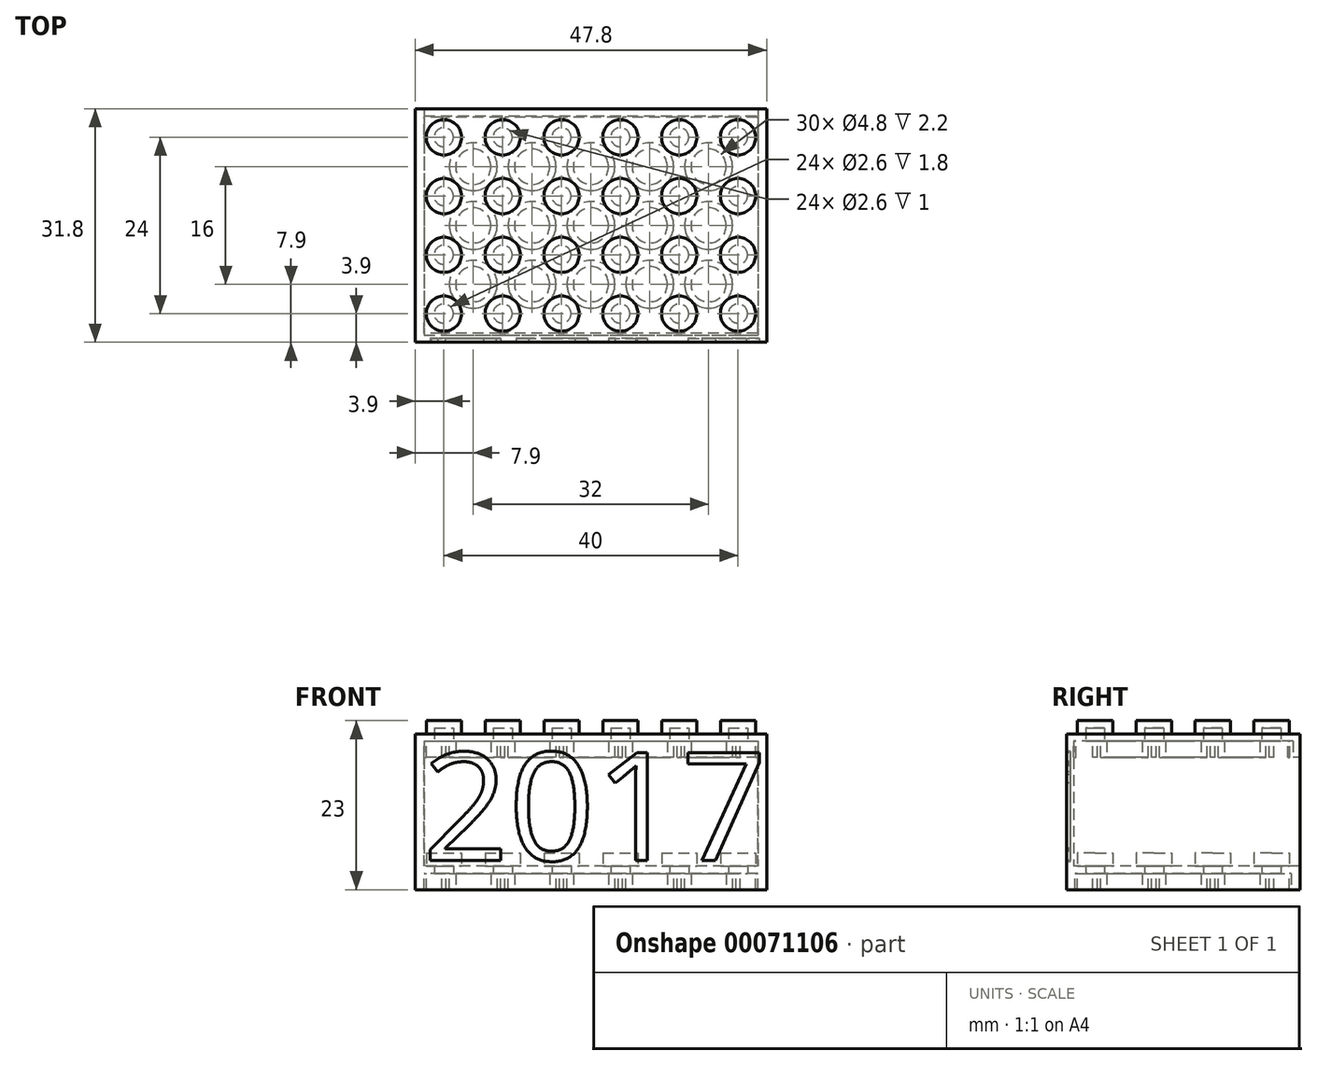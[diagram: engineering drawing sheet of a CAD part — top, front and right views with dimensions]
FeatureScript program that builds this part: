
annotation { "Feature Type Name" : "Feature", "Feature Type Description" : "" }
export const myFeature = defineFeature(function(context is Context, id is Id, definition is map)
    precondition{}
    {
        {
            var Q0;
            Q0=qCreatedBy(makeId("Top.planeOp"),FACE);
            var sketch = newSketch(context, id + "F0", { "sketchPlane" : qUnion([Q0])});
            skLineSegment(sketch, "E0.rect.bottom", {"start": v(23.9, 15.9) * mm, "end": v(-23.9, 15.9) * mm});
            skLineSegment(sketch, "E0.rect.top", {"start": v(23.9, -15.9) * mm, "end": v(-23.9, -15.9) * mm});
            skLineSegment(sketch, "E0.rect.left", {"start": v(23.9, 15.9) * mm, "end": v(23.9, -15.9) * mm});
            skLineSegment(sketch, "E0.rect.right", {"start": v(-23.9, 15.9) * mm, "end": v(-23.9, -15.9) * mm});
            skPoint(sketch, "E0.rect.middle", {"position": v(0, 0) * mm});
            skSolve(sketch);
        }
        {
            var Q0;
            Q0 = qSketchRegion(id + "F0", true);
            extrude(context, id + "F1", {"entities" : qUnion([Q0]), "depth" : 21.2 * mm});
        }
        {
            var Q0;
            Q0=makeQuery(id+"F1.opExtrude","CAP_FACE",FACE,{"disambiguationData":[OSD([sQuery(id+"F0.wireOp",EDGE,"E0.rect.bottom"),sQuery(id+"F0.wireOp",EDGE,"E0.rect.top"),sQuery(id+"F0.wireOp",EDGE,"E0.rect.left"),sQuery(id+"F0.wireOp",EDGE,"E0.rect.right")])],"isStart":false});
            var sketch = newSketch(context, id + "F2", { "sketchPlane" : qUnion([Q0])});
            skCircle(sketch, "E1", {"center": v(-20, 12) * mm, "radius": 2.4 * mm});
            skCircle(sketch, "E2.0.1.0", {"center": v(-20, 4) * mm, "radius": 2.4 * mm});
            skCircle(sketch, "E2.0.2.0", {"center": v(-20, -4) * mm, "radius": 2.4 * mm});
            skCircle(sketch, "E2.0.3.0", {"center": v(-20, -12) * mm, "radius": 2.4 * mm});
            skCircle(sketch, "E2.1.0.0", {"center": v(-12, 12) * mm, "radius": 2.4 * mm});
            skCircle(sketch, "E2.1.1.0", {"center": v(-12, 4) * mm, "radius": 2.4 * mm});
            skCircle(sketch, "E2.1.2.0", {"center": v(-12, -4) * mm, "radius": 2.4 * mm});
            skCircle(sketch, "E2.1.3.0", {"center": v(-12, -12) * mm, "radius": 2.4 * mm});
            skCircle(sketch, "E2.2.0.0", {"center": v(-4, 12) * mm, "radius": 2.4 * mm});
            skCircle(sketch, "E2.2.1.0", {"center": v(-4, 4) * mm, "radius": 2.4 * mm});
            skCircle(sketch, "E2.2.2.0", {"center": v(-4, -4) * mm, "radius": 2.4 * mm});
            skCircle(sketch, "E2.2.3.0", {"center": v(-4, -12) * mm, "radius": 2.4 * mm});
            skCircle(sketch, "E2.3.0.0", {"center": v(4, 12) * mm, "radius": 2.4 * mm});
            skCircle(sketch, "E2.3.1.0", {"center": v(4, 4) * mm, "radius": 2.4 * mm});
            skCircle(sketch, "E2.3.2.0", {"center": v(4, -4) * mm, "radius": 2.4 * mm});
            skCircle(sketch, "E2.3.3.0", {"center": v(4, -12) * mm, "radius": 2.4 * mm});
            skCircle(sketch, "E2.4.0.0", {"center": v(12, 12) * mm, "radius": 2.4 * mm});
            skCircle(sketch, "E2.4.1.0", {"center": v(12, 4) * mm, "radius": 2.4 * mm});
            skCircle(sketch, "E2.4.2.0", {"center": v(12, -4) * mm, "radius": 2.4 * mm});
            skCircle(sketch, "E2.4.3.0", {"center": v(12, -12) * mm, "radius": 2.4 * mm});
            skCircle(sketch, "E2.5.0.0", {"center": v(20, 12) * mm, "radius": 2.4 * mm});
            skCircle(sketch, "E2.5.1.0", {"center": v(20, 4) * mm, "radius": 2.4 * mm});
            skCircle(sketch, "E2.5.2.0", {"center": v(20, -4) * mm, "radius": 2.4 * mm});
            skCircle(sketch, "E2.5.3.0", {"center": v(20, -12) * mm, "radius": 2.4 * mm});
            skLineSegment(sketch, "E2.direction1", {"start": v(-20, 12) * mm, "end": v(-12, 12) * mm, "construction": true});
            skLineSegment(sketch, "E2.direction2", {"start": v(-20, 12) * mm, "end": v(-20, 4) * mm, "construction": true});
            skLineSegment(sketch, "E3", {"start": v(-12, 12) * mm, "end": v(-20, 4) * mm, "construction": true});
            skLineSegment(sketch, "E4", {"start": v(-4, 12) * mm, "end": v(-20, -4) * mm, "construction": true});
            skLineSegment(sketch, "E5", {"start": v(4, 12) * mm, "end": v(-20, -12) * mm, "construction": true});
            skLineSegment(sketch, "E6", {"start": v(12, 12) * mm, "end": v(-12, -12) * mm, "construction": true});
            skLineSegment(sketch, "E7", {"start": v(20, 12) * mm, "end": v(-4, -12) * mm, "construction": true});
            skLineSegment(sketch, "E8", {"start": v(20, 4) * mm, "end": v(4, -12) * mm, "construction": true});
            skLineSegment(sketch, "E9", {"start": v(20, -4) * mm, "end": v(12, -12) * mm, "construction": true});
            skLineSegment(sketch, "E10", {"start": v(20, 4) * mm, "end": v(12, 12) * mm, "construction": true});
            skLineSegment(sketch, "E11", {"start": v(20, -4) * mm, "end": v(4, 12) * mm, "construction": true});
            skLineSegment(sketch, "E12", {"start": v(20, -12) * mm, "end": v(-4, 12) * mm, "construction": true});
            skLineSegment(sketch, "E13", {"start": v(12, -12) * mm, "end": v(-12, 12) * mm, "construction": true});
            skLineSegment(sketch, "E14", {"start": v(4, -12) * mm, "end": v(-20, 12) * mm, "construction": true});
            skLineSegment(sketch, "E15", {"start": v(-4, -12) * mm, "end": v(-20, 4) * mm, "construction": true});
            skLineSegment(sketch, "E16", {"start": v(-12, -12) * mm, "end": v(-20, -4) * mm, "construction": true});
            skLineSegment(sketch, "E17", {"start": v(20, 12) * mm, "end": v(-38.07, 12) * mm, "construction": true});
            skLineSegment(sketch, "E18", {"start": v(-38.07, 12) * mm, "end": v(32, 12) * mm, "construction": true});
            skLineSegment(sketch, "E19", {"start": v(32, 12) * mm, "end": v(20, 12) * mm, "construction": true});
            skLineSegment(sketch, "E20", {"start": v(20, -12) * mm, "end": v(20, 35.87) * mm, "construction": true});
            skLineSegment(sketch, "E21", {"start": v(20, 35.87) * mm, "end": v(20, -18.4) * mm, "construction": true});
            skLineSegment(sketch, "E22", {"start": v(20, -18.4) * mm, "end": v(20, -12) * mm, "construction": true});
            skLineSegment(sketch, "E23", {"start": v(20, -12) * mm, "end": v(-45.19, -12) * mm, "construction": true});
            skLineSegment(sketch, "E24", {"start": v(-45.19, -12) * mm, "end": v(30.07, -12) * mm, "construction": true});
            skLineSegment(sketch, "E25", {"start": v(30.07, -12) * mm, "end": v(20, -12) * mm, "construction": true});
            skLineSegment(sketch, "E26", {"start": v(20, -4) * mm, "end": v(-32.13, -4) * mm, "construction": true});
            skLineSegment(sketch, "E27", {"start": v(-32.13, -4) * mm, "end": v(29.65, -4) * mm, "construction": true});
            skLineSegment(sketch, "E28", {"start": v(29.65, -4) * mm, "end": v(20, -4) * mm, "construction": true});
            skLineSegment(sketch, "E29", {"start": v(20, 4) * mm, "end": v(-52.97, 4) * mm, "construction": true});
            skLineSegment(sketch, "E30", {"start": v(-52.97, 4) * mm, "end": v(40.27, 4) * mm, "construction": true});
            skLineSegment(sketch, "E31", {"start": v(40.27, 4) * mm, "end": v(20, 4) * mm, "construction": true});
            skLineSegment(sketch, "E32", {"start": v(12, 12) * mm, "end": v(12, -18.88) * mm, "construction": true});
            skLineSegment(sketch, "E33", {"start": v(12, -18.88) * mm, "end": v(12, 25.65) * mm, "construction": true});
            skLineSegment(sketch, "E34", {"start": v(12, 25.65) * mm, "end": v(12, 12) * mm, "construction": true});
            skLineSegment(sketch, "E35", {"start": v(4, 12) * mm, "end": v(4, -22.99) * mm, "construction": true});
            skLineSegment(sketch, "E36", {"start": v(4, -22.99) * mm, "end": v(4, 30.25) * mm, "construction": true});
            skLineSegment(sketch, "E37", {"start": v(4, 30.25) * mm, "end": v(4, 12) * mm, "construction": true});
            skLineSegment(sketch, "E38", {"start": v(-4, 12) * mm, "end": v(-4, -21.1) * mm, "construction": true});
            skLineSegment(sketch, "E39", {"start": v(-4, -21.1) * mm, "end": v(-4, 37.53) * mm, "construction": true});
            skLineSegment(sketch, "E40", {"start": v(-4, 37.53) * mm, "end": v(-4, 12) * mm, "construction": true});
            skLineSegment(sketch, "E41", {"start": v(-12, 12) * mm, "end": v(-12, -21.86) * mm, "construction": true});
            skLineSegment(sketch, "E42", {"start": v(-12, -21.86) * mm, "end": v(-12, 28.01) * mm, "construction": true});
            skLineSegment(sketch, "E43", {"start": v(-12, 28.01) * mm, "end": v(-12, 12) * mm, "construction": true});
            skLineSegment(sketch, "E44", {"start": v(-20, 12) * mm, "end": v(-20, -23.6) * mm, "construction": true});
            skLineSegment(sketch, "E45", {"start": v(-20, -23.6) * mm, "end": v(-20, 37.01) * mm, "construction": true});
            skSolve(sketch);
        }
        {
            var Q0;
            Q0 = qSketchRegion(id + "F2", true);
            extrude(context, id + "F3", {"entities" : qUnion([Q0]), "operationType" : NewBodyOperationType.ADD, "depth" : 1.8 * mm});
        }
        {
            var Q0;
            Q0=makeQuery(id+"F1.opExtrude","SWEPT_FACE",FACE,{"disambiguationData":[OSD([sQuery(id+"F0.wireOp",EDGE,"E0.rect.top")])]});
            var sketch = newSketch(context, id + "F4", { "sketchPlane" : qUnion([Q0])});
            skLineSegment(sketch, "E46.bottom", {"start": v(-22.7, 18) * mm, "end": v(22.7, 18) * mm});
            skLineSegment(sketch, "E46.top", {"start": v(-22.7, 3.2) * mm, "end": v(22.7, 3.2) * mm});
            skLineSegment(sketch, "E46.left", {"start": v(-22.7, 18) * mm, "end": v(-22.7, 3.2) * mm});
            skLineSegment(sketch, "E46.right", {"start": v(22.7, 18) * mm, "end": v(22.7, 3.2) * mm});
            skSolve(sketch);
        }
        {
            var Q0;
            Q0 = qSketchRegion(id + "F4", true);
            extrude(context, id + "F5", {"entities" : qUnion([Q0]), "operationType" : NewBodyOperationType.REMOVE, "endBound" : BoundingType.UP_TO_NEXT, "oppositeDirection" : true, "depth" : 25 * mm});
        }
        {
            var Q0;
            Q0=makeQuery(id+"F5.boolean.opBoolean","COPY",FACE,{"derivedFrom":makeQuery(id+"F5.opExtrude","SWEPT_FACE",FACE,{"disambiguationData":[OSD([sQuery(id+"F4.wireOp",EDGE,"E46.bottom")])]})});
            var sketch = newSketch(context, id + "F6", { "sketchPlane" : qUnion([Q0])});
            skLineSegment(sketch, "E47.bottom", {"start": v(-22.7, 14.9) * mm, "end": v(22.7, 14.9) * mm});
            skLineSegment(sketch, "E47.top", {"start": v(-22.7, -14.9) * mm, "end": v(22.7, -14.9) * mm});
            skLineSegment(sketch, "E47.left", {"start": v(-22.7, 14.9) * mm, "end": v(-22.7, -14.9) * mm});
            skLineSegment(sketch, "E47.right", {"start": v(22.7, 14.9) * mm, "end": v(22.7, -14.9) * mm});
            skSolve(sketch);
        }
        {
            var Q0;
            Q0 = qSketchRegion(id + "F6", true);
            extrude(context, id + "F7", {"entities" : qUnion([Q0]), "operationType" : NewBodyOperationType.REMOVE, "oppositeDirection" : true, "depth" : 2.2 * mm});
        }
        {
            var Q0;
            Q0=makeQuery(id+"F7.boolean.opBoolean","COPY",FACE,{"derivedFrom":makeQuery(id+"F7.opExtrude","CAP_FACE",FACE,{"disambiguationData":[OSD([sQuery(id+"F6.wireOp",EDGE,"E47.bottom"),sQuery(id+"F6.wireOp",EDGE,"E47.top"),sQuery(id+"F6.wireOp",EDGE,"E47.left"),sQuery(id+"F6.wireOp",EDGE,"E47.right")])],"isStart":false})});
            var sketch = newSketch(context, id + "F8", { "sketchPlane" : qUnion([Q0])});
            skCircle(sketch, "E48", {"center": v(-20, 12) * mm, "radius": 1.3 * mm});
            skCircle(sketch, "E49.0.1.0", {"center": v(-20, 4) * mm, "radius": 1.3 * mm});
            skCircle(sketch, "E49.0.2.0", {"center": v(-20, -4) * mm, "radius": 1.3 * mm});
            skCircle(sketch, "E49.0.3.0", {"center": v(-20, -12) * mm, "radius": 1.3 * mm});
            skCircle(sketch, "E49.1.0.0", {"center": v(-12, 12) * mm, "radius": 1.3 * mm});
            skCircle(sketch, "E49.1.1.0", {"center": v(-12, 4) * mm, "radius": 1.3 * mm});
            skCircle(sketch, "E49.1.2.0", {"center": v(-12, -4) * mm, "radius": 1.3 * mm});
            skCircle(sketch, "E49.1.3.0", {"center": v(-12, -12) * mm, "radius": 1.3 * mm});
            skCircle(sketch, "E49.2.0.0", {"center": v(-4, 12) * mm, "radius": 1.3 * mm});
            skCircle(sketch, "E49.2.1.0", {"center": v(-4, 4) * mm, "radius": 1.3 * mm});
            skCircle(sketch, "E49.2.2.0", {"center": v(-4, -4) * mm, "radius": 1.3 * mm});
            skCircle(sketch, "E49.2.3.0", {"center": v(-4, -12) * mm, "radius": 1.3 * mm});
            skCircle(sketch, "E49.3.0.0", {"center": v(4, 12) * mm, "radius": 1.3 * mm});
            skCircle(sketch, "E49.3.1.0", {"center": v(4, 4) * mm, "radius": 1.3 * mm});
            skCircle(sketch, "E49.3.2.0", {"center": v(4, -4) * mm, "radius": 1.3 * mm});
            skCircle(sketch, "E49.3.3.0", {"center": v(4, -12) * mm, "radius": 1.3 * mm});
            skCircle(sketch, "E49.4.0.0", {"center": v(12, 12) * mm, "radius": 1.3 * mm});
            skCircle(sketch, "E49.4.1.0", {"center": v(12, 4) * mm, "radius": 1.3 * mm});
            skCircle(sketch, "E49.4.2.0", {"center": v(12, -4) * mm, "radius": 1.3 * mm});
            skCircle(sketch, "E49.4.3.0", {"center": v(12, -12) * mm, "radius": 1.3 * mm});
            skCircle(sketch, "E49.5.0.0", {"center": v(20, 12) * mm, "radius": 1.3 * mm});
            skCircle(sketch, "E49.5.1.0", {"center": v(20, 4) * mm, "radius": 1.3 * mm});
            skCircle(sketch, "E49.5.2.0", {"center": v(20, -4) * mm, "radius": 1.3 * mm});
            skCircle(sketch, "E49.5.3.0", {"center": v(20, -12) * mm, "radius": 1.3 * mm});
            skLineSegment(sketch, "E49.direction1", {"start": v(-20, 12) * mm, "end": v(-12, 12) * mm, "construction": true});
            skLineSegment(sketch, "E49.direction2", {"start": v(-20, 12) * mm, "end": v(-20, 4) * mm, "construction": true});
            skSolve(sketch);
        }
        {
            var Q0;
            Q0 = qSketchRegion(id + "F8", true);
            extrude(context, id + "F9", {"entities" : qUnion([Q0]), "operationType" : NewBodyOperationType.REMOVE, "oppositeDirection" : true, "depth" : 1.8 * mm});
        }
        {
            var Q0;
            Q0=makeQuery(id+"F5.boolean.opBoolean","COPY",FACE,{"derivedFrom":makeQuery(id+"F5.opExtrude","SWEPT_FACE",FACE,{"disambiguationData":[OSD([sQuery(id+"F4.wireOp",EDGE,"E46.top")])]})});
            var sketch = newSketch(context, id + "F10", { "sketchPlane" : qUnion([Q0])});
            skCircle(sketch, "E50", {"center": v(-20, 12) * mm, "radius": 2.4 * mm});
            skCircle(sketch, "E51.0.1.0", {"center": v(-20, 4) * mm, "radius": 2.4 * mm});
            skCircle(sketch, "E51.0.2.0", {"center": v(-20, -4) * mm, "radius": 2.4 * mm});
            skCircle(sketch, "E51.0.3.0", {"center": v(-20, -12) * mm, "radius": 2.4 * mm});
            skCircle(sketch, "E51.1.0.0", {"center": v(-12, 12) * mm, "radius": 2.4 * mm});
            skCircle(sketch, "E51.1.1.0", {"center": v(-12, 4) * mm, "radius": 2.4 * mm});
            skCircle(sketch, "E51.1.2.0", {"center": v(-12, -4) * mm, "radius": 2.4 * mm});
            skCircle(sketch, "E51.1.3.0", {"center": v(-12, -12) * mm, "radius": 2.4 * mm});
            skCircle(sketch, "E51.2.0.0", {"center": v(-4, 12) * mm, "radius": 2.4 * mm});
            skCircle(sketch, "E51.2.1.0", {"center": v(-4, 4) * mm, "radius": 2.4 * mm});
            skCircle(sketch, "E51.2.2.0", {"center": v(-4, -4) * mm, "radius": 2.4 * mm});
            skCircle(sketch, "E51.2.3.0", {"center": v(-4, -12) * mm, "radius": 2.4 * mm});
            skCircle(sketch, "E51.3.0.0", {"center": v(4, 12) * mm, "radius": 2.4 * mm});
            skCircle(sketch, "E51.3.1.0", {"center": v(4, 4) * mm, "radius": 2.4 * mm});
            skCircle(sketch, "E51.3.2.0", {"center": v(4, -4) * mm, "radius": 2.4 * mm});
            skCircle(sketch, "E51.3.3.0", {"center": v(4, -12) * mm, "radius": 2.4 * mm});
            skCircle(sketch, "E51.4.0.0", {"center": v(12, 12) * mm, "radius": 2.4 * mm});
            skCircle(sketch, "E51.4.1.0", {"center": v(12, 4) * mm, "radius": 2.4 * mm});
            skCircle(sketch, "E51.4.2.0", {"center": v(12, -4) * mm, "radius": 2.4 * mm});
            skCircle(sketch, "E51.4.3.0", {"center": v(12, -12) * mm, "radius": 2.4 * mm});
            skCircle(sketch, "E51.5.0.0", {"center": v(20, 12) * mm, "radius": 2.4 * mm});
            skCircle(sketch, "E51.5.1.0", {"center": v(20, 4) * mm, "radius": 2.4 * mm});
            skCircle(sketch, "E51.5.2.0", {"center": v(20, -4) * mm, "radius": 2.4 * mm});
            skCircle(sketch, "E51.5.3.0", {"center": v(20, -12) * mm, "radius": 2.4 * mm});
            skLineSegment(sketch, "E51.direction1", {"start": v(-20, 12) * mm, "end": v(-12, 12) * mm, "construction": true});
            skLineSegment(sketch, "E51.direction2", {"start": v(-20, 12) * mm, "end": v(-20, 4) * mm, "construction": true});
            skSolve(sketch);
        }
        {
            var Q0;
            Q0 = qSketchRegion(id + "F10", true);
            extrude(context, id + "F11", {"entities" : qUnion([Q0]), "operationType" : NewBodyOperationType.ADD, "depth" : 1.8 * mm});
        }
        {
            var Q0;
            Q0=makeQuery(id+"F1.opExtrude","CAP_FACE",FACE,{"disambiguationData":[OSD([sQuery(id+"F0.wireOp",EDGE,"E0.rect.bottom"),sQuery(id+"F0.wireOp",EDGE,"E0.rect.top"),sQuery(id+"F0.wireOp",EDGE,"E0.rect.left"),sQuery(id+"F0.wireOp",EDGE,"E0.rect.right")])],"isStart":true});
            var sketch = newSketch(context, id + "F12", { "sketchPlane" : qUnion([Q0])});
            skLineSegment(sketch, "E52.rect.bottom", {"start": v(22.7, 14.7) * mm, "end": v(-22.7, 14.7) * mm});
            skLineSegment(sketch, "E52.rect.top", {"start": v(22.7, -14.7) * mm, "end": v(-22.7, -14.7) * mm});
            skLineSegment(sketch, "E52.rect.left", {"start": v(22.7, 14.7) * mm, "end": v(22.7, -14.7) * mm});
            skLineSegment(sketch, "E52.rect.right", {"start": v(-22.7, 14.7) * mm, "end": v(-22.7, -14.7) * mm});
            skPoint(sketch, "E52.rect.middle", {"position": v(0, 0) * mm});
            skSolve(sketch);
        }
        {
            var Q0;
            Q0 = qSketchRegion(id + "F12", true);
            extrude(context, id + "F13", {"entities" : qUnion([Q0]), "operationType" : NewBodyOperationType.REMOVE, "oppositeDirection" : true, "depth" : 2.2 * mm});
        }
        {
            var Q0;
            Q0=makeQuery(id+"F13.boolean.opBoolean","COPY",FACE,{"derivedFrom":makeQuery(id+"F13.opExtrude","CAP_FACE",FACE,{"disambiguationData":[OSD([sQuery(id+"F12.wireOp",EDGE,"E52.rect.bottom"),sQuery(id+"F12.wireOp",EDGE,"E52.rect.top"),sQuery(id+"F12.wireOp",EDGE,"E52.rect.left"),sQuery(id+"F12.wireOp",EDGE,"E52.rect.right")])],"isStart":false})});
            var sketch = newSketch(context, id + "F14", { "sketchPlane" : qUnion([Q0])});
            skCircle(sketch, "E53", {"center": v(-20, 12) * mm, "radius": 1.3 * mm});
            skCircle(sketch, "E54.0.1.0", {"center": v(-20, 4) * mm, "radius": 1.3 * mm});
            skCircle(sketch, "E54.0.2.0", {"center": v(-20, -4) * mm, "radius": 1.3 * mm});
            skCircle(sketch, "E54.0.3.0", {"center": v(-20, -12) * mm, "radius": 1.3 * mm});
            skCircle(sketch, "E54.1.0.0", {"center": v(-12, 12) * mm, "radius": 1.3 * mm});
            skCircle(sketch, "E54.1.1.0", {"center": v(-12, 4) * mm, "radius": 1.3 * mm});
            skCircle(sketch, "E54.1.2.0", {"center": v(-12, -4) * mm, "radius": 1.3 * mm});
            skCircle(sketch, "E54.1.3.0", {"center": v(-12, -12) * mm, "radius": 1.3 * mm});
            skCircle(sketch, "E54.2.0.0", {"center": v(-4, 12) * mm, "radius": 1.3 * mm});
            skCircle(sketch, "E54.2.1.0", {"center": v(-4, 4) * mm, "radius": 1.3 * mm});
            skCircle(sketch, "E54.2.2.0", {"center": v(-4, -4) * mm, "radius": 1.3 * mm});
            skCircle(sketch, "E54.2.3.0", {"center": v(-4, -12) * mm, "radius": 1.3 * mm});
            skCircle(sketch, "E54.3.0.0", {"center": v(4, 12) * mm, "radius": 1.3 * mm});
            skCircle(sketch, "E54.3.1.0", {"center": v(4, 4) * mm, "radius": 1.3 * mm});
            skCircle(sketch, "E54.3.2.0", {"center": v(4, -4) * mm, "radius": 1.3 * mm});
            skCircle(sketch, "E54.3.3.0", {"center": v(4, -12) * mm, "radius": 1.3 * mm});
            skCircle(sketch, "E54.4.0.0", {"center": v(12, 12) * mm, "radius": 1.3 * mm});
            skCircle(sketch, "E54.4.1.0", {"center": v(12, 4) * mm, "radius": 1.3 * mm});
            skCircle(sketch, "E54.4.2.0", {"center": v(12, -4) * mm, "radius": 1.3 * mm});
            skCircle(sketch, "E54.4.3.0", {"center": v(12, -12) * mm, "radius": 1.3 * mm});
            skCircle(sketch, "E54.5.0.0", {"center": v(20, 12) * mm, "radius": 1.3 * mm});
            skCircle(sketch, "E54.5.1.0", {"center": v(20, 4) * mm, "radius": 1.3 * mm});
            skCircle(sketch, "E54.5.2.0", {"center": v(20, -4) * mm, "radius": 1.3 * mm});
            skCircle(sketch, "E54.5.3.0", {"center": v(20, -12) * mm, "radius": 1.3 * mm});
            skLineSegment(sketch, "E54.direction1", {"start": v(-20, 12) * mm, "end": v(-12, 12) * mm, "construction": true});
            skLineSegment(sketch, "E54.direction2", {"start": v(-20, 12) * mm, "end": v(-20, 4) * mm, "construction": true});
            skLineSegment(sketch, "E55", {"start": v(4, -12) * mm, "end": v(-20, 12) * mm, "construction": true});
            skLineSegment(sketch, "E56", {"start": v(-4, -12) * mm, "end": v(-20, 4) * mm, "construction": true});
            skLineSegment(sketch, "E57", {"start": v(-12, -12) * mm, "end": v(-20, -4) * mm, "construction": true});
            skLineSegment(sketch, "E58", {"start": v(12, -12) * mm, "end": v(-12, 12) * mm, "construction": true});
            skLineSegment(sketch, "E59", {"start": v(20, -12) * mm, "end": v(-4, 12) * mm, "construction": true});
            skLineSegment(sketch, "E60", {"start": v(20, -4) * mm, "end": v(4, 12) * mm, "construction": true});
            skLineSegment(sketch, "E61", {"start": v(20, 4) * mm, "end": v(12, 12) * mm, "construction": true});
            skLineSegment(sketch, "E62", {"start": v(20, -4) * mm, "end": v(12, -12) * mm, "construction": true});
            skLineSegment(sketch, "E63", {"start": v(20, 4) * mm, "end": v(4, -12) * mm, "construction": true});
            skLineSegment(sketch, "E64", {"start": v(-4, -12) * mm, "end": v(20, 12) * mm, "construction": true});
            skLineSegment(sketch, "E65", {"start": v(12, 12) * mm, "end": v(-12, -12) * mm, "construction": true});
            skLineSegment(sketch, "E66", {"start": v(4, 12) * mm, "end": v(-20, -12) * mm, "construction": true});
            skLineSegment(sketch, "E67", {"start": v(-4, 12) * mm, "end": v(-20, -4) * mm, "construction": true});
            skLineSegment(sketch, "E68", {"start": v(-12, 12) * mm, "end": v(-20, 4) * mm, "construction": true});
            skLineSegment(sketch, "E69", {"start": v(20, 12) * mm, "end": v(20, -28.9) * mm, "construction": true});
            skLineSegment(sketch, "E70", {"start": v(20, -28.9) * mm, "end": v(20, 24.52) * mm, "construction": true});
            skLineSegment(sketch, "E71", {"start": v(20, 24.52) * mm, "end": v(20, 12) * mm, "construction": true});
            skLineSegment(sketch, "E72", {"start": v(20, 12) * mm, "end": v(33.5, 12) * mm, "construction": true});
            skLineSegment(sketch, "E73", {"start": v(33.5, 12) * mm, "end": v(-36.68, 12) * mm, "construction": true});
            skLineSegment(sketch, "E74", {"start": v(-36.68, 12) * mm, "end": v(-20, 12) * mm, "construction": true});
            skLineSegment(sketch, "E75", {"start": v(-20, -12) * mm, "end": v(-20, 29.78) * mm, "construction": true});
            skLineSegment(sketch, "E76", {"start": v(-20, 29.78) * mm, "end": v(-20, -28.36) * mm, "construction": true});
            skLineSegment(sketch, "E77", {"start": v(-20, -28.36) * mm, "end": v(-20, -12) * mm, "construction": true});
            skLineSegment(sketch, "E78", {"start": v(-12, -12) * mm, "end": v(-12, -28.37) * mm, "construction": true});
            skLineSegment(sketch, "E79", {"start": v(-12, -28.37) * mm, "end": v(-12, 25.53) * mm, "construction": true});
            skLineSegment(sketch, "E80", {"start": v(-12, 25.53) * mm, "end": v(-12, 12) * mm, "construction": true});
            skLineSegment(sketch, "E81", {"start": v(-4, 12) * mm, "end": v(-4, 29.87) * mm, "construction": true});
            skLineSegment(sketch, "E82", {"start": v(-4, 29.87) * mm, "end": v(-4, -29.44) * mm, "construction": true});
            skLineSegment(sketch, "E83", {"start": v(-4, -29.44) * mm, "end": v(-4, -12) * mm, "construction": true});
            skLineSegment(sketch, "E84", {"start": v(4, -12) * mm, "end": v(4, -26.66) * mm, "construction": true});
            skLineSegment(sketch, "E85", {"start": v(4, -26.66) * mm, "end": v(4, 25.49) * mm, "construction": true});
            skLineSegment(sketch, "E86", {"start": v(4, 25.49) * mm, "end": v(4, 12) * mm, "construction": true});
            skLineSegment(sketch, "E87", {"start": v(12, 12) * mm, "end": v(12, -30.83) * mm, "construction": true});
            skLineSegment(sketch, "E88", {"start": v(12, -30.83) * mm, "end": v(12, 29.44) * mm, "construction": true});
            skLineSegment(sketch, "E89", {"start": v(20, 4) * mm, "end": v(-33.7, 4) * mm, "construction": true});
            skLineSegment(sketch, "E90", {"start": v(-33.7, 4) * mm, "end": v(31.82, 4) * mm, "construction": true});
            skLineSegment(sketch, "E91", {"start": v(31.82, 4) * mm, "end": v(20, 4) * mm, "construction": true});
            skLineSegment(sketch, "E92", {"start": v(20, -4) * mm, "end": v(33.95, -4) * mm, "construction": true});
            skLineSegment(sketch, "E93", {"start": v(33.95, -4) * mm, "end": v(-39.5, -4) * mm, "construction": true});
            skLineSegment(sketch, "E94", {"start": v(-39.5, -4) * mm, "end": v(-20, -4) * mm, "construction": true});
            skLineSegment(sketch, "E95", {"start": v(-20, -12) * mm, "end": v(-41.56, -12) * mm, "construction": true});
            skLineSegment(sketch, "E96", {"start": v(-41.56, -12) * mm, "end": v(30.77, -12) * mm, "construction": true});
            skSolve(sketch);
        }
        {
            var Q0;
            Q0 = qSketchRegion(id + "F14", true);
            extrude(context, id + "F15", {"entities" : qUnion([Q0]), "operationType" : NewBodyOperationType.REMOVE, "oppositeDirection" : true, "depth" : 1 * mm});
        }
        {
            var Q0;
            Q0=makeQuery(id+"F14.imprint","IMPRINT",FACE,{"disambiguationData":[TD([[makeQuery(id+"F14.imprint","IMPRINT",EDGE,{"derivedFrom":sQuery(id+"F14.wireOp",EDGE,"E53")}),-1.0]])]});
            var sketch = newSketch(context, id + "F16", { "sketchPlane" : qUnion([Q0])});
            skCircle(sketch, "E97", {"center": v(-16, 8) * mm, "radius": 3.25 * mm});
            skCircle(sketch, "E98.0.1.0", {"center": v(-16, 0) * mm, "radius": 3.25 * mm});
            skCircle(sketch, "E98.0.2.0", {"center": v(-16, -8) * mm, "radius": 3.25 * mm});
            skCircle(sketch, "E98.1.0.0", {"center": v(-8, 8) * mm, "radius": 3.25 * mm});
            skCircle(sketch, "E98.1.1.0", {"center": v(-8, 0) * mm, "radius": 3.25 * mm});
            skCircle(sketch, "E98.1.2.0", {"center": v(-8, -8) * mm, "radius": 3.25 * mm});
            skCircle(sketch, "E98.2.0.0", {"center": v(0, 8) * mm, "radius": 3.25 * mm});
            skCircle(sketch, "E98.2.1.0", {"center": v(0, 0) * mm, "radius": 3.25 * mm});
            skCircle(sketch, "E98.2.2.0", {"center": v(0, -8) * mm, "radius": 3.25 * mm});
            skCircle(sketch, "E98.3.0.0", {"center": v(8, 8) * mm, "radius": 3.25 * mm});
            skCircle(sketch, "E98.3.1.0", {"center": v(8, 0) * mm, "radius": 3.25 * mm});
            skCircle(sketch, "E98.3.2.0", {"center": v(8, -8) * mm, "radius": 3.25 * mm});
            skCircle(sketch, "E98.4.0.0", {"center": v(16, 8) * mm, "radius": 3.25 * mm});
            skCircle(sketch, "E98.4.1.0", {"center": v(16, 0) * mm, "radius": 3.25 * mm});
            skCircle(sketch, "E98.4.2.0", {"center": v(16, -8) * mm, "radius": 3.25 * mm});
            skLineSegment(sketch, "E98.direction1", {"start": v(-16, 8) * mm, "end": v(-8, 8) * mm, "construction": true});
            skLineSegment(sketch, "E98.direction2", {"start": v(-16, 8) * mm, "end": v(-16, 0) * mm, "construction": true});
            skSolve(sketch);
        }
        {
            var Q0;
            Q0 = qSketchRegion(id + "F16", true);
            var Q1;
            Q1=qCreatedBy(makeId("Top.planeOp"),FACE);
            extrude(context, id + "F17", {"entities" : qUnion([Q0]), "operationType" : NewBodyOperationType.ADD, "endBound" : BoundingType.UP_TO_SURFACE, "endBoundEntityFace" : qUnion([Q1]), "depth" : 25 * mm});
        }
        {
            var Q0;
            Q0=makeQuery(id+"F17.opExtrude","CAP_FACE",FACE,{"disambiguationData":[OSD([sQuery(id+"F16.wireOp",EDGE,"E98.1.0.0")])],"isStart":false});
            var sketch = newSketch(context, id + "F18", { "sketchPlane" : qUnion([Q0])});
            skCircle(sketch, "E99", {"center": v(-16, 8) * mm, "radius": 2.4 * mm});
            skCircle(sketch, "E100.0.1.0", {"center": v(-16, 0) * mm, "radius": 2.4 * mm});
            skCircle(sketch, "E100.0.2.0", {"center": v(-16, -8) * mm, "radius": 2.4 * mm});
            skCircle(sketch, "E100.1.0.0", {"center": v(-8, 8) * mm, "radius": 2.4 * mm});
            skCircle(sketch, "E100.1.1.0", {"center": v(-8, 0) * mm, "radius": 2.4 * mm});
            skCircle(sketch, "E100.1.2.0", {"center": v(-8, -8) * mm, "radius": 2.4 * mm});
            skCircle(sketch, "E100.2.0.0", {"center": v(0, 8) * mm, "radius": 2.4 * mm});
            skCircle(sketch, "E100.2.1.0", {"center": v(0, 0) * mm, "radius": 2.4 * mm});
            skCircle(sketch, "E100.2.2.0", {"center": v(0, -8) * mm, "radius": 2.4 * mm});
            skCircle(sketch, "E100.3.0.0", {"center": v(8, 8) * mm, "radius": 2.4 * mm});
            skCircle(sketch, "E100.3.1.0", {"center": v(8, 0) * mm, "radius": 2.4 * mm});
            skCircle(sketch, "E100.3.2.0", {"center": v(8, -8) * mm, "radius": 2.4 * mm});
            skCircle(sketch, "E100.4.0.0", {"center": v(16, 8) * mm, "radius": 2.4 * mm});
            skCircle(sketch, "E100.4.1.0", {"center": v(16, 0) * mm, "radius": 2.4 * mm});
            skCircle(sketch, "E100.4.2.0", {"center": v(16, -8) * mm, "radius": 2.4 * mm});
            skLineSegment(sketch, "E100.direction1", {"start": v(-16, 8) * mm, "end": v(-8, 8) * mm, "construction": true});
            skLineSegment(sketch, "E100.direction2", {"start": v(-16, 8) * mm, "end": v(-16, 0) * mm, "construction": true});
            skSolve(sketch);
        }
        {
            var Q0;
            Q0 = qSketchRegion(id + "F18", true);
            extrude(context, id + "F19", {"entities" : qUnion([Q0]), "operationType" : NewBodyOperationType.REMOVE, "oppositeDirection" : true, "depth" : 2.2 * mm});
        }
        {
            var Q0;
            Q0=makeQuery(id+"F7.boolean.opBoolean","COPY",FACE,{"derivedFrom":makeQuery(id+"F7.opExtrude","CAP_FACE",FACE,{"disambiguationData":[OSD([sQuery(id+"F6.wireOp",EDGE,"E47.bottom"),sQuery(id+"F6.wireOp",EDGE,"E47.top"),sQuery(id+"F6.wireOp",EDGE,"E47.left"),sQuery(id+"F6.wireOp",EDGE,"E47.right")])],"isStart":false})});
            var sketch = newSketch(context, id + "F20", { "sketchPlane" : qUnion([Q0])});
            skCircle(sketch, "E101", {"center": v(-16, 8) * mm, "radius": 3.25 * mm});
            skCircle(sketch, "E102.0.1.0", {"center": v(-16, 0) * mm, "radius": 3.25 * mm});
            skCircle(sketch, "E102.0.2.0", {"center": v(-16, -8) * mm, "radius": 3.25 * mm});
            skCircle(sketch, "E102.1.0.0", {"center": v(-8, 8) * mm, "radius": 3.25 * mm});
            skCircle(sketch, "E102.1.1.0", {"center": v(-8, 0) * mm, "radius": 3.25 * mm});
            skCircle(sketch, "E102.1.2.0", {"center": v(-8, -8) * mm, "radius": 3.25 * mm});
            skCircle(sketch, "E102.2.0.0", {"center": v(0, 8) * mm, "radius": 3.25 * mm});
            skCircle(sketch, "E102.2.1.0", {"center": v(0, 0) * mm, "radius": 3.25 * mm});
            skCircle(sketch, "E102.2.2.0", {"center": v(0, -8) * mm, "radius": 3.25 * mm});
            skCircle(sketch, "E102.3.0.0", {"center": v(8, 8) * mm, "radius": 3.25 * mm});
            skCircle(sketch, "E102.3.1.0", {"center": v(8, 0) * mm, "radius": 3.25 * mm});
            skCircle(sketch, "E102.3.2.0", {"center": v(8, -8) * mm, "radius": 3.25 * mm});
            skCircle(sketch, "E102.4.0.0", {"center": v(16, 8) * mm, "radius": 3.25 * mm});
            skCircle(sketch, "E102.4.1.0", {"center": v(16, 0) * mm, "radius": 3.25 * mm});
            skCircle(sketch, "E102.4.2.0", {"center": v(16, -8) * mm, "radius": 3.25 * mm});
            skLineSegment(sketch, "E102.direction1", {"start": v(-16, 8) * mm, "end": v(-8, 8) * mm, "construction": true});
            skLineSegment(sketch, "E102.direction2", {"start": v(-16, 8) * mm, "end": v(-16, 0) * mm, "construction": true});
            skSolve(sketch);
        }
        {
            var Q0;
            Q0 = qSketchRegion(id + "F20", true);
            extrude(context, id + "F21", {"entities" : qUnion([Q0]), "operationType" : NewBodyOperationType.ADD, "depth" : 2.2 * mm});
        }
        {
            var Q0;
            Q0=makeQuery(id+"F21.opExtrude","CAP_FACE",FACE,{"disambiguationData":[OSD([sQuery(id+"F20.wireOp",EDGE,"E101")])],"isStart":false});
            var sketch = newSketch(context, id + "F22", { "sketchPlane" : qUnion([Q0])});
            skCircle(sketch, "E103", {"center": v(-16, 8) * mm, "radius": 2.4 * mm});
            skCircle(sketch, "E104.0.1.0", {"center": v(-16, 0) * mm, "radius": 2.4 * mm});
            skCircle(sketch, "E104.0.2.0", {"center": v(-16, -8) * mm, "radius": 2.4 * mm});
            skCircle(sketch, "E104.1.0.0", {"center": v(-8, 8) * mm, "radius": 2.4 * mm});
            skCircle(sketch, "E104.1.1.0", {"center": v(-8, 0) * mm, "radius": 2.4 * mm});
            skCircle(sketch, "E104.1.2.0", {"center": v(-8, -8) * mm, "radius": 2.4 * mm});
            skCircle(sketch, "E104.2.0.0", {"center": v(0, 8) * mm, "radius": 2.4 * mm});
            skCircle(sketch, "E104.2.1.0", {"center": v(0, 0) * mm, "radius": 2.4 * mm});
            skCircle(sketch, "E104.2.2.0", {"center": v(0, -8) * mm, "radius": 2.4 * mm});
            skCircle(sketch, "E104.3.0.0", {"center": v(8, 8) * mm, "radius": 2.4 * mm});
            skCircle(sketch, "E104.3.1.0", {"center": v(8, 0) * mm, "radius": 2.4 * mm});
            skCircle(sketch, "E104.3.2.0", {"center": v(8, -8) * mm, "radius": 2.4 * mm});
            skCircle(sketch, "E104.4.0.0", {"center": v(16, 8) * mm, "radius": 2.4 * mm});
            skCircle(sketch, "E104.4.1.0", {"center": v(16, 0) * mm, "radius": 2.4 * mm});
            skCircle(sketch, "E104.4.2.0", {"center": v(16, -8) * mm, "radius": 2.4 * mm});
            skLineSegment(sketch, "E104.direction1", {"start": v(-16, 8) * mm, "end": v(-8, 8) * mm, "construction": true});
            skLineSegment(sketch, "E104.direction2", {"start": v(-16, 8) * mm, "end": v(-16, 0) * mm, "construction": true});
            skSolve(sketch);
        }
        {
            var Q0;
            Q0 = qSketchRegion(id + "F22", true);
            extrude(context, id + "F23", {"entities" : qUnion([Q0]), "operationType" : NewBodyOperationType.REMOVE, "oppositeDirection" : true, "depth" : 2.2 * mm});
        }
        {
            var Q0;
            Q0=makeQuery(id+"F7.boolean.opBoolean","SPLIT",FACE,{"disambiguationData":[TD([makeQuery(id+"F1.opExtrude","SWEPT_FACE",FACE,{"disambiguationData":[OSD([sQuery(id+"F0.wireOp",EDGE,"E0.rect.top")])]})])],"derivedFrom":makeQuery(id+"F5.boolean.opBoolean","COPY",FACE,{"derivedFrom":makeQuery(id+"F5.opExtrude","SWEPT_FACE",FACE,{"disambiguationData":[OSD([sQuery(id+"F4.wireOp",EDGE,"E46.bottom")])]})})});
            var sketch = newSketch(context, id + "F24", { "sketchPlane" : qUnion([Q0])});
            skLineSegment(sketch, "E105.bottom", {"start": v(-22.7, 15.9) * mm, "end": v(22.7, 15.9) * mm});
            skLineSegment(sketch, "E105.top", {"start": v(-22.7, 14.9) * mm, "end": v(22.7, 14.9) * mm});
            skLineSegment(sketch, "E105.left", {"start": v(-22.7, 15.9) * mm, "end": v(-22.7, 14.9) * mm});
            skLineSegment(sketch, "E105.right", {"start": v(22.7, 15.9) * mm, "end": v(22.7, 14.9) * mm});
            skSolve(sketch);
        }
        {
            var Q0;
            Q0 = qSketchRegion(id + "F24", true);
            var Q1;
            Q1=makeQuery(id+"F5.boolean.opBoolean","COPY",FACE,{"derivedFrom":makeQuery(id+"F5.opExtrude","SWEPT_FACE",FACE,{"disambiguationData":[OSD([sQuery(id+"F4.wireOp",EDGE,"E46.top")])]})});
            extrude(context, id + "F25", {"entities" : qUnion([Q0]), "operationType" : NewBodyOperationType.ADD, "endBound" : BoundingType.UP_TO_SURFACE, "endBoundEntityFace" : qUnion([Q1]), "depth" : 25 * mm});
        }
        {
            var Q0;
            Q0=makeQuery(id+"F25.boolean.opBoolean","MERGE",FACE,{"derivedFrom":[makeQuery(id+"F1.opExtrude","SWEPT_FACE",FACE,{"disambiguationData":[OSD([sQuery(id+"F0.wireOp",EDGE,"E0.rect.top")])]}),makeQuery(id+"F25.opExtrude","SWEPT_FACE",FACE,{"disambiguationData":[OSD([sQuery(id+"F24.wireOp",EDGE,"E105.bottom")])]})]});
            var sketch = newSketch(context, id + "F26", { "sketchPlane" : qUnion([Q0])});
            skText(sketch, "E106", { "text": "2017", "fontName": "OpenSans-Regular.ttf"});
            const initialGuessF26  = {"E106": [-0.0229, 0.004, 1, 0, 0.01475]};
            skSetInitialGuess(sketch, initialGuessF26);
            skSolve(sketch);
        }
        {
            var Q0;
            Q0 = qSketchRegion(id + "F26", true);
            extrude(context, id + "F27", {"entities" : qUnion([Q0]), "operationType" : NewBodyOperationType.REMOVE, "oppositeDirection" : true, "depth" : .5 * mm});
        }
        {
            var Q0;
            Q0=makeQuery(id+"F13.boolean.opBoolean","COPY",FACE,{"derivedFrom":makeQuery(id+"F13.opExtrude","CAP_FACE",FACE,{"disambiguationData":[OSD([sQuery(id+"F12.wireOp",EDGE,"E52.rect.bottom"),sQuery(id+"F12.wireOp",EDGE,"E52.rect.top"),sQuery(id+"F12.wireOp",EDGE,"E52.rect.left"),sQuery(id+"F12.wireOp",EDGE,"E52.rect.right")])],"isStart":false})});
            var sketch = newSketch(context, id + "F28", { "sketchPlane" : qUnion([Q0])});
            skLineSegment(sketch, "E107.bottom", {"start": v(20.3, -14.7) * mm, "end": v(19.7, -14.7) * mm});
            skLineSegment(sketch, "E107.top", {"start": v(20.3, -14.4) * mm, "end": v(19.7, -14.4) * mm});
            skLineSegment(sketch, "E107.left", {"start": v(20.3, -14.7) * mm, "end": v(20.3, -14.4) * mm});
            skLineSegment(sketch, "E107.right", {"start": v(19.7, -14.7) * mm, "end": v(19.7, -14.4) * mm});
            skLineSegment(sketch, "E108.0.1.0", {"start": v(20.3, 14.7) * mm, "end": v(19.7, 14.7) * mm});
            skLineSegment(sketch, "E108.0.1.1", {"start": v(19.7, 14.4) * mm, "end": v(19.7, 14.7) * mm});
            skLineSegment(sketch, "E108.0.1.2", {"start": v(20.3, 14.4) * mm, "end": v(19.7, 14.4) * mm});
            skLineSegment(sketch, "E108.0.1.3", {"start": v(20.3, 14.4) * mm, "end": v(20.3, 14.7) * mm});
            skLineSegment(sketch, "E108.1.0.0", {"start": v(12.3, -14.4) * mm, "end": v(11.7, -14.4) * mm});
            skLineSegment(sketch, "E108.1.0.1", {"start": v(11.7, -14.7) * mm, "end": v(11.7, -14.4) * mm});
            skLineSegment(sketch, "E108.1.0.2", {"start": v(12.3, -14.7) * mm, "end": v(11.7, -14.7) * mm});
            skLineSegment(sketch, "E108.1.0.3", {"start": v(12.3, -14.7) * mm, "end": v(12.3, -14.4) * mm});
            skLineSegment(sketch, "E108.1.1.0", {"start": v(12.3, 14.7) * mm, "end": v(11.7, 14.7) * mm});
            skLineSegment(sketch, "E108.1.1.1", {"start": v(11.7, 14.4) * mm, "end": v(11.7, 14.7) * mm});
            skLineSegment(sketch, "E108.1.1.2", {"start": v(12.3, 14.4) * mm, "end": v(11.7, 14.4) * mm});
            skLineSegment(sketch, "E108.1.1.3", {"start": v(12.3, 14.4) * mm, "end": v(12.3, 14.7) * mm});
            skLineSegment(sketch, "E108.2.0.0", {"start": v(4.3, -14.4) * mm, "end": v(3.7, -14.4) * mm});
            skLineSegment(sketch, "E108.2.0.1", {"start": v(3.7, -14.7) * mm, "end": v(3.7, -14.4) * mm});
            skLineSegment(sketch, "E108.2.0.2", {"start": v(4.3, -14.7) * mm, "end": v(3.7, -14.7) * mm});
            skLineSegment(sketch, "E108.2.0.3", {"start": v(4.3, -14.7) * mm, "end": v(4.3, -14.4) * mm});
            skLineSegment(sketch, "E108.2.1.0", {"start": v(4.3, 14.7) * mm, "end": v(3.7, 14.7) * mm});
            skLineSegment(sketch, "E108.2.1.1", {"start": v(3.7, 14.4) * mm, "end": v(3.7, 14.7) * mm});
            skLineSegment(sketch, "E108.2.1.2", {"start": v(4.3, 14.4) * mm, "end": v(3.7, 14.4) * mm});
            skLineSegment(sketch, "E108.2.1.3", {"start": v(4.3, 14.4) * mm, "end": v(4.3, 14.7) * mm});
            skLineSegment(sketch, "E108.3.0.0", {"start": v(-3.7, -14.4) * mm, "end": v(-4.3, -14.4) * mm});
            skLineSegment(sketch, "E108.3.0.1", {"start": v(-4.3, -14.7) * mm, "end": v(-4.3, -14.4) * mm});
            skLineSegment(sketch, "E108.3.0.2", {"start": v(-3.7, -14.7) * mm, "end": v(-4.3, -14.7) * mm});
            skLineSegment(sketch, "E108.3.0.3", {"start": v(-3.7, -14.7) * mm, "end": v(-3.7, -14.4) * mm});
            skLineSegment(sketch, "E108.3.1.0", {"start": v(-3.7, 14.7) * mm, "end": v(-4.3, 14.7) * mm});
            skLineSegment(sketch, "E108.3.1.1", {"start": v(-4.3, 14.4) * mm, "end": v(-4.3, 14.7) * mm});
            skLineSegment(sketch, "E108.3.1.2", {"start": v(-3.7, 14.4) * mm, "end": v(-4.3, 14.4) * mm});
            skLineSegment(sketch, "E108.3.1.3", {"start": v(-3.7, 14.4) * mm, "end": v(-3.7, 14.7) * mm});
            skLineSegment(sketch, "E108.4.0.0", {"start": v(-11.7, -14.4) * mm, "end": v(-12.3, -14.4) * mm});
            skLineSegment(sketch, "E108.4.0.1", {"start": v(-12.3, -14.7) * mm, "end": v(-12.3, -14.4) * mm});
            skLineSegment(sketch, "E108.4.0.2", {"start": v(-11.7, -14.7) * mm, "end": v(-12.3, -14.7) * mm});
            skLineSegment(sketch, "E108.4.0.3", {"start": v(-11.7, -14.7) * mm, "end": v(-11.7, -14.4) * mm});
            skLineSegment(sketch, "E108.4.1.0", {"start": v(-11.7, 14.7) * mm, "end": v(-12.3, 14.7) * mm});
            skLineSegment(sketch, "E108.4.1.1", {"start": v(-12.3, 14.4) * mm, "end": v(-12.3, 14.7) * mm});
            skLineSegment(sketch, "E108.4.1.2", {"start": v(-11.7, 14.4) * mm, "end": v(-12.3, 14.4) * mm});
            skLineSegment(sketch, "E108.4.1.3", {"start": v(-11.7, 14.4) * mm, "end": v(-11.7, 14.7) * mm});
            skLineSegment(sketch, "E108.5.0.0", {"start": v(-19.7, -14.4) * mm, "end": v(-20.3, -14.4) * mm});
            skLineSegment(sketch, "E108.5.0.1", {"start": v(-20.3, -14.7) * mm, "end": v(-20.3, -14.4) * mm});
            skLineSegment(sketch, "E108.5.0.2", {"start": v(-19.7, -14.7) * mm, "end": v(-20.3, -14.7) * mm});
            skLineSegment(sketch, "E108.5.0.3", {"start": v(-19.7, -14.7) * mm, "end": v(-19.7, -14.4) * mm});
            skLineSegment(sketch, "E108.5.1.0", {"start": v(-19.7, 14.7) * mm, "end": v(-20.3, 14.7) * mm});
            skLineSegment(sketch, "E108.5.1.1", {"start": v(-20.3, 14.4) * mm, "end": v(-20.3, 14.7) * mm});
            skLineSegment(sketch, "E108.5.1.2", {"start": v(-19.7, 14.4) * mm, "end": v(-20.3, 14.4) * mm});
            skLineSegment(sketch, "E108.5.1.3", {"start": v(-19.7, 14.4) * mm, "end": v(-19.7, 14.7) * mm});
            skLineSegment(sketch, "E108.direction1", {"start": v(19.7, -14.4) * mm, "end": v(11.7, -14.4) * mm, "construction": true});
            skLineSegment(sketch, "E108.direction2", {"start": v(19.7, -14.4) * mm, "end": v(19.7, 14.7) * mm, "construction": true});
            skSolve(sketch);
        }
        {
            var Q0;
            Q0 = qSketchRegion(id + "F28", true);
            var Q1;
            Q1=qCreatedBy(makeId("Top.planeOp"),FACE);
            extrude(context, id + "F29", {"entities" : qUnion([Q0]), "operationType" : NewBodyOperationType.ADD, "endBound" : BoundingType.UP_TO_SURFACE, "endBoundEntityFace" : qUnion([Q1]), "depth" : 2.2 * mm});
        }
        {
            var Q0;
            Q0=makeQuery(id+"F14.imprint","IMPRINT",FACE,{"disambiguationData":[TD([[makeQuery(id+"F14.imprint","IMPRINT",EDGE,{"derivedFrom":sQuery(id+"F14.wireOp",EDGE,"E53")}),-1.0]])]});
            var sketch = newSketch(context, id + "F30", { "sketchPlane" : qUnion([Q0])});
            skLineSegment(sketch, "E109.bottom", {"start": v(22.4, 12.3) * mm, "end": v(22.7, 12.3) * mm});
            skLineSegment(sketch, "E109.top", {"start": v(22.4, 11.7) * mm, "end": v(22.7, 11.7) * mm});
            skLineSegment(sketch, "E109.left", {"start": v(22.4, 12.3) * mm, "end": v(22.4, 11.7) * mm});
            skLineSegment(sketch, "E109.right", {"start": v(22.7, 12.3) * mm, "end": v(22.7, 11.7) * mm});
            skLineSegment(sketch, "E110.0.1.0", {"start": v(22.4, 4.3) * mm, "end": v(22.7, 4.3) * mm});
            skLineSegment(sketch, "E110.0.1.1", {"start": v(22.4, 4.3) * mm, "end": v(22.4, 3.7) * mm});
            skLineSegment(sketch, "E110.0.1.2", {"start": v(22.4, 3.7) * mm, "end": v(22.7, 3.7) * mm});
            skLineSegment(sketch, "E110.0.1.3", {"start": v(22.7, 4.3) * mm, "end": v(22.7, 3.7) * mm});
            skLineSegment(sketch, "E110.0.2.0", {"start": v(22.4, -3.7) * mm, "end": v(22.7, -3.7) * mm});
            skLineSegment(sketch, "E110.0.2.1", {"start": v(22.4, -3.7) * mm, "end": v(22.4, -4.3) * mm});
            skLineSegment(sketch, "E110.0.2.2", {"start": v(22.4, -4.3) * mm, "end": v(22.7, -4.3) * mm});
            skLineSegment(sketch, "E110.0.2.3", {"start": v(22.7, -3.7) * mm, "end": v(22.7, -4.3) * mm});
            skLineSegment(sketch, "E110.0.3.0", {"start": v(22.4, -11.7) * mm, "end": v(22.7, -11.7) * mm});
            skLineSegment(sketch, "E110.0.3.1", {"start": v(22.4, -11.7) * mm, "end": v(22.4, -12.3) * mm});
            skLineSegment(sketch, "E110.0.3.2", {"start": v(22.4, -12.3) * mm, "end": v(22.7, -12.3) * mm});
            skLineSegment(sketch, "E110.0.3.3", {"start": v(22.7, -11.7) * mm, "end": v(22.7, -12.3) * mm});
            skLineSegment(sketch, "E110.1.0.0", {"start": v(-22.7, 12.3) * mm, "end": v(-22.4, 12.3) * mm});
            skLineSegment(sketch, "E110.1.0.1", {"start": v(-22.7, 12.3) * mm, "end": v(-22.7, 11.7) * mm});
            skLineSegment(sketch, "E110.1.0.2", {"start": v(-22.7, 11.7) * mm, "end": v(-22.4, 11.7) * mm});
            skLineSegment(sketch, "E110.1.0.3", {"start": v(-22.4, 12.3) * mm, "end": v(-22.4, 11.7) * mm});
            skLineSegment(sketch, "E110.1.1.0", {"start": v(-22.7, 4.3) * mm, "end": v(-22.4, 4.3) * mm});
            skLineSegment(sketch, "E110.1.1.1", {"start": v(-22.7, 4.3) * mm, "end": v(-22.7, 3.7) * mm});
            skLineSegment(sketch, "E110.1.1.2", {"start": v(-22.7, 3.7) * mm, "end": v(-22.4, 3.7) * mm});
            skLineSegment(sketch, "E110.1.1.3", {"start": v(-22.4, 4.3) * mm, "end": v(-22.4, 3.7) * mm});
            skLineSegment(sketch, "E110.1.2.0", {"start": v(-22.7, -3.7) * mm, "end": v(-22.4, -3.7) * mm});
            skLineSegment(sketch, "E110.1.2.1", {"start": v(-22.7, -3.7) * mm, "end": v(-22.7, -4.3) * mm});
            skLineSegment(sketch, "E110.1.2.2", {"start": v(-22.7, -4.3) * mm, "end": v(-22.4, -4.3) * mm});
            skLineSegment(sketch, "E110.1.2.3", {"start": v(-22.4, -3.7) * mm, "end": v(-22.4, -4.3) * mm});
            skLineSegment(sketch, "E110.1.3.0", {"start": v(-22.7, -11.7) * mm, "end": v(-22.4, -11.7) * mm});
            skLineSegment(sketch, "E110.1.3.1", {"start": v(-22.7, -11.7) * mm, "end": v(-22.7, -12.3) * mm});
            skLineSegment(sketch, "E110.1.3.2", {"start": v(-22.7, -12.3) * mm, "end": v(-22.4, -12.3) * mm});
            skLineSegment(sketch, "E110.1.3.3", {"start": v(-22.4, -11.7) * mm, "end": v(-22.4, -12.3) * mm});
            skLineSegment(sketch, "E110.direction1", {"start": v(22.4, 12.3) * mm, "end": v(-22.7, 12.3) * mm, "construction": true});
            skLineSegment(sketch, "E110.direction2", {"start": v(22.4, 12.3) * mm, "end": v(22.4, 4.3) * mm, "construction": true});
            skSolve(sketch);
        }
        {
            var Q0;
            Q0 = qSketchRegion(id + "F30", true);
            var Q1;
            Q1=qCreatedBy(makeId("Top.planeOp"),FACE);
            extrude(context, id + "F31", {"entities" : qUnion([Q0]), "operationType" : NewBodyOperationType.ADD, "endBound" : BoundingType.UP_TO_SURFACE, "endBoundEntityFace" : qUnion([Q1]), "depth" : 25 * mm});
        }
        {
            var Q0;
            Q0=makeQuery(id+"F7.boolean.opBoolean","COPY",FACE,{"derivedFrom":makeQuery(id+"F7.opExtrude","CAP_FACE",FACE,{"disambiguationData":[OSD([sQuery(id+"F6.wireOp",EDGE,"E47.bottom"),sQuery(id+"F6.wireOp",EDGE,"E47.top"),sQuery(id+"F6.wireOp",EDGE,"E47.left"),sQuery(id+"F6.wireOp",EDGE,"E47.right")])],"isStart":false})});
            var sketch = newSketch(context, id + "F32", { "sketchPlane" : qUnion([Q0])});
            skLineSegment(sketch, "E111.bottom", {"start": v(22.4, -12.3) * mm, "end": v(22.7, -12.3) * mm});
            skLineSegment(sketch, "E111.top", {"start": v(22.4, -11.7) * mm, "end": v(22.7, -11.7) * mm});
            skLineSegment(sketch, "E111.left", {"start": v(22.4, -12.3) * mm, "end": v(22.4, -11.7) * mm});
            skLineSegment(sketch, "E111.right", {"start": v(22.7, -12.3) * mm, "end": v(22.7, -11.7) * mm});
            skLineSegment(sketch, "E112.0.1.0", {"start": v(22.4, -3.7) * mm, "end": v(22.7, -3.7) * mm});
            skLineSegment(sketch, "E112.0.1.1", {"start": v(22.7, -4.3) * mm, "end": v(22.7, -3.7) * mm});
            skLineSegment(sketch, "E112.0.1.2", {"start": v(22.4, -4.3) * mm, "end": v(22.7, -4.3) * mm});
            skLineSegment(sketch, "E112.0.1.3", {"start": v(22.4, -4.3) * mm, "end": v(22.4, -3.7) * mm});
            skLineSegment(sketch, "E112.0.2.0", {"start": v(22.4, 4.3) * mm, "end": v(22.7, 4.3) * mm});
            skLineSegment(sketch, "E112.0.2.1", {"start": v(22.7, 3.7) * mm, "end": v(22.7, 4.3) * mm});
            skLineSegment(sketch, "E112.0.2.2", {"start": v(22.4, 3.7) * mm, "end": v(22.7, 3.7) * mm});
            skLineSegment(sketch, "E112.0.2.3", {"start": v(22.4, 3.7) * mm, "end": v(22.4, 4.3) * mm});
            skLineSegment(sketch, "E112.0.3.0", {"start": v(22.4, 12.3) * mm, "end": v(22.7, 12.3) * mm});
            skLineSegment(sketch, "E112.0.3.1", {"start": v(22.7, 11.7) * mm, "end": v(22.7, 12.3) * mm});
            skLineSegment(sketch, "E112.0.3.2", {"start": v(22.4, 11.7) * mm, "end": v(22.7, 11.7) * mm});
            skLineSegment(sketch, "E112.0.3.3", {"start": v(22.4, 11.7) * mm, "end": v(22.4, 12.3) * mm});
            skLineSegment(sketch, "E112.1.0.0", {"start": v(-22.7, -11.7) * mm, "end": v(-22.4, -11.7) * mm});
            skLineSegment(sketch, "E112.1.0.1", {"start": v(-22.4, -12.3) * mm, "end": v(-22.4, -11.7) * mm});
            skLineSegment(sketch, "E112.1.0.2", {"start": v(-22.7, -12.3) * mm, "end": v(-22.4, -12.3) * mm});
            skLineSegment(sketch, "E112.1.0.3", {"start": v(-22.7, -12.3) * mm, "end": v(-22.7, -11.7) * mm});
            skLineSegment(sketch, "E112.1.1.0", {"start": v(-22.7, -3.7) * mm, "end": v(-22.4, -3.7) * mm});
            skLineSegment(sketch, "E112.1.1.1", {"start": v(-22.4, -4.3) * mm, "end": v(-22.4, -3.7) * mm});
            skLineSegment(sketch, "E112.1.1.2", {"start": v(-22.7, -4.3) * mm, "end": v(-22.4, -4.3) * mm});
            skLineSegment(sketch, "E112.1.1.3", {"start": v(-22.7, -4.3) * mm, "end": v(-22.7, -3.7) * mm});
            skLineSegment(sketch, "E112.1.2.0", {"start": v(-22.7, 4.3) * mm, "end": v(-22.4, 4.3) * mm});
            skLineSegment(sketch, "E112.1.2.1", {"start": v(-22.4, 3.7) * mm, "end": v(-22.4, 4.3) * mm});
            skLineSegment(sketch, "E112.1.2.2", {"start": v(-22.7, 3.7) * mm, "end": v(-22.4, 3.7) * mm});
            skLineSegment(sketch, "E112.1.2.3", {"start": v(-22.7, 3.7) * mm, "end": v(-22.7, 4.3) * mm});
            skLineSegment(sketch, "E112.1.3.0", {"start": v(-22.7, 12.3) * mm, "end": v(-22.4, 12.3) * mm});
            skLineSegment(sketch, "E112.1.3.1", {"start": v(-22.4, 11.7) * mm, "end": v(-22.4, 12.3) * mm});
            skLineSegment(sketch, "E112.1.3.2", {"start": v(-22.7, 11.7) * mm, "end": v(-22.4, 11.7) * mm});
            skLineSegment(sketch, "E112.1.3.3", {"start": v(-22.7, 11.7) * mm, "end": v(-22.7, 12.3) * mm});
            skLineSegment(sketch, "E112.direction1", {"start": v(22.4, -11.7) * mm, "end": v(-22.7, -11.7) * mm, "construction": true});
            skLineSegment(sketch, "E112.direction2", {"start": v(22.4, -11.7) * mm, "end": v(22.4, -3.7) * mm, "construction": true});
            skSolve(sketch);
        }
        {
            var Q0;
            Q0 = qSketchRegion(id + "F32", true);
            extrude(context, id + "F33", {"entities" : qUnion([Q0]), "operationType" : NewBodyOperationType.ADD, "depth" : 2.2 * mm});
        }
        {
            var Q0;
            Q0=makeQuery(id+"F7.boolean.opBoolean","COPY",FACE,{"derivedFrom":makeQuery(id+"F7.opExtrude","CAP_FACE",FACE,{"disambiguationData":[OSD([sQuery(id+"F6.wireOp",EDGE,"E47.bottom"),sQuery(id+"F6.wireOp",EDGE,"E47.top"),sQuery(id+"F6.wireOp",EDGE,"E47.left"),sQuery(id+"F6.wireOp",EDGE,"E47.right")])],"isStart":false})});
            var sketch = newSketch(context, id + "F34", { "sketchPlane" : qUnion([Q0])});
            skLineSegment(sketch, "E113.bottom", {"start": v(-20.3, 14.9) * mm, "end": v(-19.7, 14.9) * mm});
            skLineSegment(sketch, "E113.top", {"start": v(-20.3, 14.6) * mm, "end": v(-19.7, 14.6) * mm});
            skLineSegment(sketch, "E113.left", {"start": v(-20.3, 14.9) * mm, "end": v(-20.3, 14.6) * mm});
            skLineSegment(sketch, "E113.right", {"start": v(-19.7, 14.9) * mm, "end": v(-19.7, 14.6) * mm});
            skLineSegment(sketch, "E114.0.1.0", {"start": v(-20.3, -14.2) * mm, "end": v(-19.7, -14.2) * mm});
            skLineSegment(sketch, "E114.0.1.1", {"start": v(-20.3, -14.2) * mm, "end": v(-20.3, -14.5) * mm});
            skLineSegment(sketch, "E114.0.1.2", {"start": v(-20.3, -14.5) * mm, "end": v(-19.7, -14.5) * mm});
            skLineSegment(sketch, "E114.0.1.3", {"start": v(-19.7, -14.2) * mm, "end": v(-19.7, -14.5) * mm});
            skLineSegment(sketch, "E114.1.0.0", {"start": v(-12.3, 14.9) * mm, "end": v(-11.7, 14.9) * mm});
            skLineSegment(sketch, "E114.1.0.1", {"start": v(-12.3, 14.9) * mm, "end": v(-12.3, 14.6) * mm});
            skLineSegment(sketch, "E114.1.0.2", {"start": v(-12.3, 14.6) * mm, "end": v(-11.7, 14.6) * mm});
            skLineSegment(sketch, "E114.1.0.3", {"start": v(-11.7, 14.9) * mm, "end": v(-11.7, 14.6) * mm});
            skLineSegment(sketch, "E114.1.1.0", {"start": v(-12.3, -14.2) * mm, "end": v(-11.7, -14.2) * mm});
            skLineSegment(sketch, "E114.1.1.1", {"start": v(-12.3, -14.2) * mm, "end": v(-12.3, -14.5) * mm});
            skLineSegment(sketch, "E114.1.1.2", {"start": v(-12.3, -14.5) * mm, "end": v(-11.7, -14.5) * mm});
            skLineSegment(sketch, "E114.1.1.3", {"start": v(-11.7, -14.2) * mm, "end": v(-11.7, -14.5) * mm});
            skLineSegment(sketch, "E114.2.0.0", {"start": v(-4.3, 14.9) * mm, "end": v(-3.7, 14.9) * mm});
            skLineSegment(sketch, "E114.2.0.1", {"start": v(-4.3, 14.9) * mm, "end": v(-4.3, 14.6) * mm});
            skLineSegment(sketch, "E114.2.0.2", {"start": v(-4.3, 14.6) * mm, "end": v(-3.7, 14.6) * mm});
            skLineSegment(sketch, "E114.2.0.3", {"start": v(-3.7, 14.9) * mm, "end": v(-3.7, 14.6) * mm});
            skLineSegment(sketch, "E114.2.1.0", {"start": v(-4.3, -14.2) * mm, "end": v(-3.7, -14.2) * mm});
            skLineSegment(sketch, "E114.2.1.1", {"start": v(-4.3, -14.2) * mm, "end": v(-4.3, -14.5) * mm});
            skLineSegment(sketch, "E114.2.1.2", {"start": v(-4.3, -14.5) * mm, "end": v(-3.7, -14.5) * mm});
            skLineSegment(sketch, "E114.2.1.3", {"start": v(-3.7, -14.2) * mm, "end": v(-3.7, -14.5) * mm});
            skLineSegment(sketch, "E114.3.0.0", {"start": v(3.7, 14.9) * mm, "end": v(4.3, 14.9) * mm});
            skLineSegment(sketch, "E114.3.0.1", {"start": v(3.7, 14.9) * mm, "end": v(3.7, 14.6) * mm});
            skLineSegment(sketch, "E114.3.0.2", {"start": v(3.7, 14.6) * mm, "end": v(4.3, 14.6) * mm});
            skLineSegment(sketch, "E114.3.0.3", {"start": v(4.3, 14.9) * mm, "end": v(4.3, 14.6) * mm});
            skLineSegment(sketch, "E114.3.1.0", {"start": v(3.7, -14.2) * mm, "end": v(4.3, -14.2) * mm});
            skLineSegment(sketch, "E114.3.1.1", {"start": v(3.7, -14.2) * mm, "end": v(3.7, -14.5) * mm});
            skLineSegment(sketch, "E114.3.1.2", {"start": v(3.7, -14.5) * mm, "end": v(4.3, -14.5) * mm});
            skLineSegment(sketch, "E114.3.1.3", {"start": v(4.3, -14.2) * mm, "end": v(4.3, -14.5) * mm});
            skLineSegment(sketch, "E114.4.0.0", {"start": v(11.7, 14.9) * mm, "end": v(12.3, 14.9) * mm});
            skLineSegment(sketch, "E114.4.0.1", {"start": v(11.7, 14.9) * mm, "end": v(11.7, 14.6) * mm});
            skLineSegment(sketch, "E114.4.0.2", {"start": v(11.7, 14.6) * mm, "end": v(12.3, 14.6) * mm});
            skLineSegment(sketch, "E114.4.0.3", {"start": v(12.3, 14.9) * mm, "end": v(12.3, 14.6) * mm});
            skLineSegment(sketch, "E114.4.1.0", {"start": v(11.7, -14.2) * mm, "end": v(12.3, -14.2) * mm});
            skLineSegment(sketch, "E114.4.1.1", {"start": v(11.7, -14.2) * mm, "end": v(11.7, -14.5) * mm});
            skLineSegment(sketch, "E114.4.1.2", {"start": v(11.7, -14.5) * mm, "end": v(12.3, -14.5) * mm});
            skLineSegment(sketch, "E114.4.1.3", {"start": v(12.3, -14.2) * mm, "end": v(12.3, -14.5) * mm});
            skLineSegment(sketch, "E114.5.0.0", {"start": v(19.7, 14.9) * mm, "end": v(20.3, 14.9) * mm});
            skLineSegment(sketch, "E114.5.0.1", {"start": v(19.7, 14.9) * mm, "end": v(19.7, 14.6) * mm});
            skLineSegment(sketch, "E114.5.0.2", {"start": v(19.7, 14.6) * mm, "end": v(20.3, 14.6) * mm});
            skLineSegment(sketch, "E114.5.0.3", {"start": v(20.3, 14.9) * mm, "end": v(20.3, 14.6) * mm});
            skLineSegment(sketch, "E114.5.1.0", {"start": v(19.7, -14.2) * mm, "end": v(20.3, -14.2) * mm});
            skLineSegment(sketch, "E114.5.1.1", {"start": v(19.7, -14.2) * mm, "end": v(19.7, -14.5) * mm});
            skLineSegment(sketch, "E114.5.1.2", {"start": v(19.7, -14.5) * mm, "end": v(20.3, -14.5) * mm});
            skLineSegment(sketch, "E114.5.1.3", {"start": v(20.3, -14.2) * mm, "end": v(20.3, -14.5) * mm});
            skLineSegment(sketch, "E114.direction1", {"start": v(-20.3, 14.9) * mm, "end": v(-12.3, 14.9) * mm, "construction": true});
            skLineSegment(sketch, "E114.direction2", {"start": v(-20.3, 14.9) * mm, "end": v(-20.3, -14.2) * mm, "construction": true});
            skSolve(sketch);
        }
        {
            var Q0;
            Q0 = qSketchRegion(id + "F34", true);
            extrude(context, id + "F35", {"entities" : qUnion([Q0]), "operationType" : NewBodyOperationType.ADD, "depth" : 2.2 * mm});
        }
    });
